# Revit family: 201_KN-_
name_source: partatom
category: Air Terminals
units: mm (PartAtom-declared; Revit-internal decimal feet)

## family parameters
Always vertical = Yes
Cut with Voids When Loaded = No
Part Type = Normal
Room Calculation Point = Yes
Round Connector Dimension = Use Diameter
Shared = No
Work Plane-Based = No

## types (7) — shared parameters
C = 12 mm  [stored 0.0393701 ft]
CAT0 = Yes
CL_Location_5000 = 5000 mm  [stored 16.4042 ft]
Description = AIR SUPPLY VALVE
GAP = 10 mm  [stored 0.0328084 ft]
L_ARR = 400 mm  [stored 1.31234 ft]
Manufacturer = Alnor
QmdConnectorList = 201;D
URL = http://www.ventilation-alnor.co.uk
W_ARR = 400 mm  [stored 1.31234 ft]
XRefLineVPlnId = 7453
YRefLineVPlnId = 7456
magiPartTypeId = 201
magiProductFamilyId = KN-*
zero-valued in all types: CLBTZ, H_ARR

## per-type parameters (varying)
| type | B | D | DP | DP1 | RB |
| KN-080 | 115 mm  [stored 0.377297 ft] | 80 mm | 32 mm  [stored 0.104987 ft] | 72 mm  [stored 0.23622 ft] | 50 mm |
| KN-250 | 302 mm | 250 mm | 100 mm  [stored 0.328084 ft] | 225 mm | 140 mm |
| KN-200 | 248 mm | 200 mm | 80 mm  [stored 0.262467 ft] | 180 mm | 114 mm |
| KN-160 | 212 mm | 160 mm | 64 mm | 144 mm | 95 mm |
| KN-150 | 202 mm | 150 mm | 60 mm | 135 mm | 90 mm |
| KN-125 | 164 mm | 125 mm | 50 mm | 113 mm | 74 mm |
| KN-100 | 137 mm | 100 mm | 40 mm | 90 mm | 61 mm |

note: column(s) folded — value = type name in every type: MC Product Code, magiProductId

note: [stored X ft] marks values corroborated as IEEE doubles in the binary element streams (Revit-internal decimal feet)

## geometry (parser evidence)
native form markers: Blend x4, Sweep x1
no freeform markers — native parametric forms only
